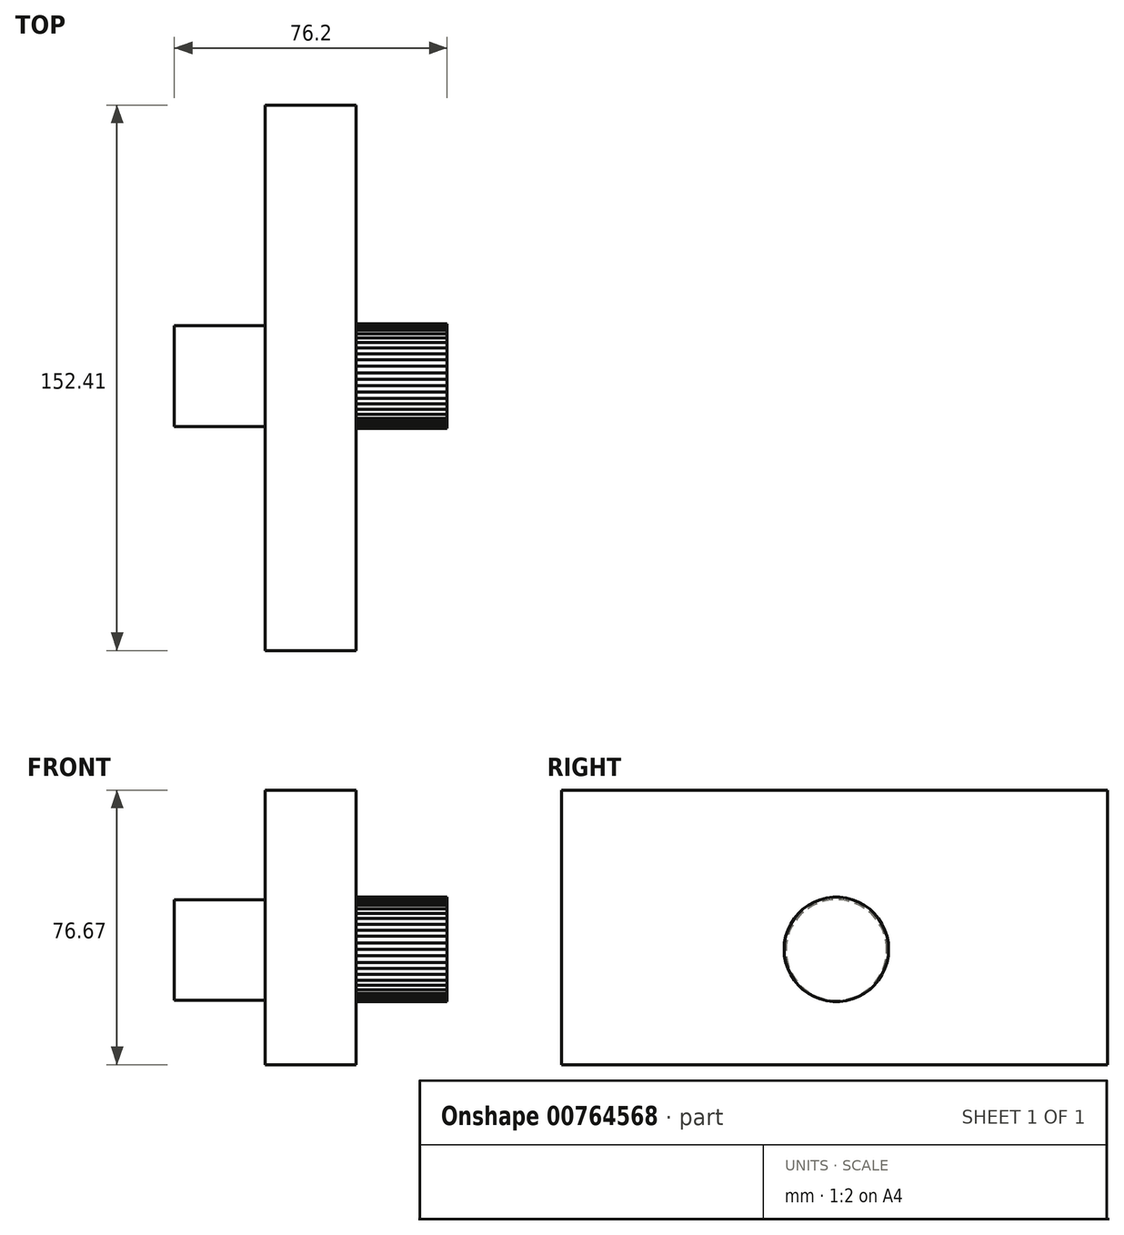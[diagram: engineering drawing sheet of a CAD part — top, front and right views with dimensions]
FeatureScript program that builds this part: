
annotation { "Feature Type Name" : "Feature", "Feature Type Description" : "" }
export const myFeature = defineFeature(function(context is Context, id is Id, definition is map)
    precondition{}
    {
        {
            var Q0;
            Q0=qCreatedBy(makeId("Right.planeOp"),FACE);
            var sketch = newSketch(context, id + "F0", { "sketchPlane" : qUnion([Q0])});
            skLineSegment(sketch, "E0.bottom", {"start": v(-8.14, 0) * mm, "end": v(75.69, 0) * mm});
            skLineSegment(sketch, "E0.top", {"start": v(-8.14, 76.67) * mm, "end": v(75.69, 76.67) * mm});
            skLineSegment(sketch, "E0.left", {"start": v(-8.14, 0) * mm, "end": v(-8.14, 76.67) * mm});
            skLineSegment(sketch, "E0.right", {"start": v(75.69, 0) * mm, "end": v(75.69, 76.67) * mm});
            skSolve(sketch);
        }
        {
            var Q0;
            Q0=makeQuery(id+"F0.imprint","IMPRINT",FACE,{"disambiguationData":[TD([[makeQuery(id+"F0.imprint","IMPRINT",EDGE,{"derivedFrom":sQuery(id+"F0.wireOp",EDGE,"E0.bottom")}),1.0]])]});
            extrude(context, id + "F1", {"entities" : qUnion([Q0]), "oppositeDirection" : true, "depth" : 25.4 * mm, "offsetDistance" : 25.4 * mm});
        }
        {
            var Q0;
            Q0=qCreatedBy(makeId("Top.planeOp"),FACE);
            var sketch = newSketch(context, id + "F2", { "sketchPlane" : qUnion([Q0])});
            skLineSegment(sketch, "E1", {"start": v(-24.68, -7.8) * mm, "end": v(-24.68, -75.66) * mm});
            skLineSegment(sketch, "E2", {"start": v(-24.68, -75.66) * mm, "end": v(0, -75.66) * mm});
            skLineSegment(sketch, "E3", {"start": v(0, -75.66) * mm, "end": v(-0.15, 0) * mm});
            skSolve(sketch);
        }
        {
            var Q0;
            Q0 = qSketchRegion(id + "F2", true);
            var Q1;
            Q1=makeQuery(id+"F1.opExtrude","SWEPT_FACE",FACE,{"disambiguationData":[OSD([sQuery(id+"F0.wireOp",EDGE,"E0.left")])]});
            extrude(context, id + "F3", {"entities" : qUnion([Q0, Q1]), "operationType" : NewBodyOperationType.ADD, "depth" : 68.58 * mm, "offsetDistance" : 25.4 * mm});
        }
        {
            var Q0;
            {var subQ0=sQuery(id+"F0.wireOp",EDGE,"E0.left");Q0=makeQuery(id+"F3.boolean.opBoolean","MERGE",FACE,{"derivedFrom":[makeQuery(id+"F1.opExtrude","CAP_FACE",FACE,{"disambiguationData":[OSD([sQuery(id+"F0.wireOp",EDGE,"E0.bottom"),sQuery(id+"F0.wireOp",EDGE,"E0.top"),subQ0,sQuery(id+"F0.wireOp",EDGE,"E0.right")])],"isStart":true}),makeQuery(id+"F3.opExtrude","SWEPT_FACE",FACE,{"disambiguationData":[OSD([subQ0]),TDD([makeQuery(id+"F1.opExtrude","CAP_EDGE",EDGE,{"disambiguationData":[OSD([subQ0])],"isStart":true})])]})]});}
            var sketch = newSketch(context, id + "F4", { "sketchPlane" : qUnion([Q0])});
            skCircle(sketch, "E4.cCircle", {"center": v(0, 32.22) * mm, "radius": 14.57 * mm, "construction": true});
            skLineSegment(sketch, "E4.0", {"start": v(-0.92, 46.79) * mm, "end": v(0.92, 46.79) * mm});
            skLineSegment(sketch, "E4.1", {"start": v(0.92, 46.79) * mm, "end": v(2.74, 46.56) * mm});
            skLineSegment(sketch, "E4.2", {"start": v(2.74, 46.56) * mm, "end": v(4.51, 46.1) * mm});
            skLineSegment(sketch, "E4.3", {"start": v(4.51, 46.1) * mm, "end": v(6.22, 45.43) * mm});
            skLineSegment(sketch, "E4.4", {"start": v(6.22, 45.43) * mm, "end": v(7.82, 44.54) * mm});
            skLineSegment(sketch, "E4.5", {"start": v(7.82, 44.54) * mm, "end": v(9.3, 43.47) * mm});
            skLineSegment(sketch, "E4.6", {"start": v(9.3, 43.47) * mm, "end": v(10.64, 42.21) * mm});
            skLineSegment(sketch, "E4.7", {"start": v(10.64, 42.21) * mm, "end": v(11.81, 40.8) * mm});
            skLineSegment(sketch, "E4.8", {"start": v(11.81, 40.8) * mm, "end": v(12.8, 39.25) * mm});
            skLineSegment(sketch, "E4.9", {"start": v(12.8, 39.25) * mm, "end": v(13.57, 37.6) * mm});
            skLineSegment(sketch, "E4.10", {"start": v(13.57, 37.6) * mm, "end": v(14.14, 35.85) * mm});
            skLineSegment(sketch, "E4.11", {"start": v(14.14, 35.85) * mm, "end": v(14.48, 34.05) * mm});
            skLineSegment(sketch, "E4.12", {"start": v(14.48, 34.05) * mm, "end": v(14.6, 32.22) * mm});
            skLineSegment(sketch, "E4.13", {"start": v(14.6, 32.22) * mm, "end": v(14.48, 30.39) * mm});
            skLineSegment(sketch, "E4.14", {"start": v(14.48, 30.39) * mm, "end": v(14.14, 28.59) * mm});
            skLineSegment(sketch, "E4.15", {"start": v(14.14, 28.59) * mm, "end": v(13.57, 26.84) * mm});
            skLineSegment(sketch, "E4.16", {"start": v(13.57, 26.84) * mm, "end": v(12.8, 25.18) * mm});
            skLineSegment(sketch, "E4.17", {"start": v(12.8, 25.18) * mm, "end": v(11.81, 23.64) * mm});
            skLineSegment(sketch, "E4.18", {"start": v(11.81, 23.64) * mm, "end": v(10.64, 22.22) * mm});
            skLineSegment(sketch, "E4.19", {"start": v(10.64, 22.22) * mm, "end": v(9.3, 20.97) * mm});
            skLineSegment(sketch, "E4.20", {"start": v(9.3, 20.97) * mm, "end": v(7.82, 19.9) * mm});
            skLineSegment(sketch, "E4.21", {"start": v(7.82, 19.9) * mm, "end": v(6.22, 19) * mm});
            skLineSegment(sketch, "E4.22", {"start": v(6.22, 19) * mm, "end": v(4.51, 18.33) * mm});
            skLineSegment(sketch, "E4.23", {"start": v(4.51, 18.33) * mm, "end": v(2.74, 17.88) * mm});
            skLineSegment(sketch, "E4.24", {"start": v(2.74, 17.88) * mm, "end": v(0.92, 17.65) * mm});
            skLineSegment(sketch, "E4.25", {"start": v(0.92, 17.65) * mm, "end": v(-0.92, 17.65) * mm});
            skLineSegment(sketch, "E4.26", {"start": v(-0.92, 17.65) * mm, "end": v(-2.74, 17.88) * mm});
            skLineSegment(sketch, "E4.27", {"start": v(-2.74, 17.88) * mm, "end": v(-4.51, 18.33) * mm});
            skLineSegment(sketch, "E4.28", {"start": v(-4.51, 18.33) * mm, "end": v(-6.22, 19) * mm});
            skLineSegment(sketch, "E4.29", {"start": v(-6.22, 19) * mm, "end": v(-7.82, 19.9) * mm});
            skLineSegment(sketch, "E4.30", {"start": v(-7.82, 19.9) * mm, "end": v(-9.3, 20.97) * mm});
            skLineSegment(sketch, "E4.31", {"start": v(-9.3, 20.97) * mm, "end": v(-10.64, 22.22) * mm});
            skLineSegment(sketch, "E4.32", {"start": v(-10.64, 22.22) * mm, "end": v(-11.81, 23.64) * mm});
            skLineSegment(sketch, "E4.33", {"start": v(-11.81, 23.64) * mm, "end": v(-12.8, 25.18) * mm});
            skLineSegment(sketch, "E4.34", {"start": v(-12.8, 25.18) * mm, "end": v(-13.57, 26.84) * mm});
            skLineSegment(sketch, "E4.35", {"start": v(-13.57, 26.84) * mm, "end": v(-14.14, 28.59) * mm});
            skLineSegment(sketch, "E4.36", {"start": v(-14.14, 28.59) * mm, "end": v(-14.48, 30.39) * mm});
            skLineSegment(sketch, "E4.37", {"start": v(-14.48, 30.39) * mm, "end": v(-14.6, 32.22) * mm});
            skLineSegment(sketch, "E4.38", {"start": v(-14.6, 32.22) * mm, "end": v(-14.48, 34.05) * mm});
            skLineSegment(sketch, "E4.39", {"start": v(-14.48, 34.05) * mm, "end": v(-14.14, 35.85) * mm});
            skLineSegment(sketch, "E4.40", {"start": v(-14.14, 35.85) * mm, "end": v(-13.57, 37.6) * mm});
            skLineSegment(sketch, "E4.41", {"start": v(-13.57, 37.6) * mm, "end": v(-12.8, 39.25) * mm});
            skLineSegment(sketch, "E4.42", {"start": v(-12.8, 39.25) * mm, "end": v(-11.81, 40.8) * mm});
            skLineSegment(sketch, "E4.43", {"start": v(-11.81, 40.8) * mm, "end": v(-10.64, 42.21) * mm});
            skLineSegment(sketch, "E4.44", {"start": v(-10.64, 42.21) * mm, "end": v(-9.3, 43.47) * mm});
            skLineSegment(sketch, "E4.45", {"start": v(-9.3, 43.47) * mm, "end": v(-7.82, 44.54) * mm});
            skLineSegment(sketch, "E4.46", {"start": v(-7.82, 44.54) * mm, "end": v(-6.22, 45.43) * mm});
            skLineSegment(sketch, "E4.47", {"start": v(-6.22, 45.43) * mm, "end": v(-4.51, 46.1) * mm});
            skLineSegment(sketch, "E4.48", {"start": v(-4.51, 46.1) * mm, "end": v(-2.74, 46.56) * mm});
            skLineSegment(sketch, "E4.49", {"start": v(-2.74, 46.56) * mm, "end": v(-0.92, 46.79) * mm});
            skPoint(sketch, "E4.0.midPoint", {"position": v(0, 46.79) * mm});
            skSolve(sketch);
        }
        {
            var Q0;
            Q0=makeQuery(id+"F4.imprint","IMPRINT",FACE,{"disambiguationData":[TD([[makeQuery(id+"F4.imprint","IMPRINT",EDGE,{"derivedFrom":sQuery(id+"F4.wireOp",EDGE,"E4.0")}),-1.0]])]});
            var sketch = newSketch(context, id + "F5", { "sketchPlane" : qUnion([Q0])});
            skSolve(sketch);
        }
        {
            var Q0;
            Q0=makeQuery(id+"F5.imprint","IMPRINT",FACE,{"disambiguationData":[TD([[makeQuery(id+"F5.imprint","IMPRINT",EDGE,{"derivedFrom":makeQuery(id+"F4.imprint","IMPRINT",EDGE,{"derivedFrom":sQuery(id+"F4.wireOp",EDGE,"E4.0")})}),-1.0]])]});
            extrude(context, id + "F6", {"entities" : qUnion([Q0]), "operationType" : NewBodyOperationType.ADD, "depth" : 25.4 * mm, "offsetDistance" : 25.4 * mm});
        }
        {
            var Q0;
            {var subQ0=sQuery(id+"F0.wireOp",EDGE,"E0.left");Q0=makeQuery(id+"F3.boolean.opBoolean","MERGE",FACE,{"derivedFrom":[makeQuery(id+"F1.opExtrude","CAP_FACE",FACE,{"disambiguationData":[OSD([sQuery(id+"F0.wireOp",EDGE,"E0.bottom"),sQuery(id+"F0.wireOp",EDGE,"E0.top"),subQ0,sQuery(id+"F0.wireOp",EDGE,"E0.right")])],"isStart":false}),makeQuery(id+"F3.opExtrude","SWEPT_FACE",FACE,{"disambiguationData":[OSD([subQ0]),TDD([makeQuery(id+"F1.opExtrude","CAP_EDGE",EDGE,{"disambiguationData":[OSD([subQ0])],"isStart":false})])]})]});}
            var sketch = newSketch(context, id + "F7", { "sketchPlane" : qUnion([Q0])});
            skCircle(sketch, "E5", {"center": v(0, 32) * mm, "radius": 14.07 * mm});
            skSolve(sketch);
        }
        {
            var Q0;
            Q0 = qSketchRegion(id + "F7", true);
            extrude(context, id + "F8", {"entities" : qUnion([Q0]), "operationType" : NewBodyOperationType.ADD, "depth" : 25.4 * mm, "offsetDistance" : 25.4 * mm});
        }
        {
            var Q0;
            {var subQ0=sQuery(id+"F0.wireOp",EDGE,"E0.top");Q0=makeQuery(id+"F3.boolean.opBoolean","MERGE",FACE,{"derivedFrom":[makeQuery(id+"F1.opExtrude","SWEPT_FACE",FACE,{"disambiguationData":[OSD([subQ0])]}),makeQuery(id+"F3.opExtrude","SWEPT_FACE",FACE,{"disambiguationData":[OSD([subQ0,sQuery(id+"F0.wireOp",EDGE,"E0.left")])]})]});}
            var sketch = newSketch(context, id + "F9", { "sketchPlane" : qUnion([Q0])});
            skSolve(sketch);
        }
    });
